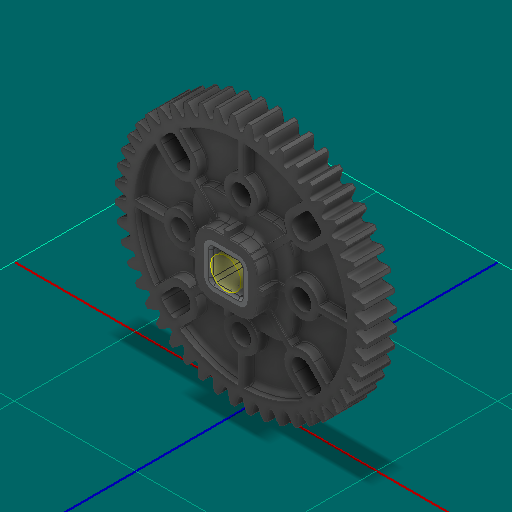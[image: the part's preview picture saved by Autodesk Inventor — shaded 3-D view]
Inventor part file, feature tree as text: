
AUTODESK INVENTOR PART (.ipt)
format: ipt  version: 2025 (Build 290162000, 162)  size: 3,893,248 bytes
history: native  units: in
note: dims shown in document units (in); Inventor stores cm internally (conversion verified against a paired STEP export)
features: other x6, sketch x3
ambient origin geometry x8: Origin, YZ Plane, XZ Plane, XY Plane, X Axis, Y Axis, Z Axis, Center Point
bodies: Solid1 (feature_tree), Solid2 (feature_tree)
feature tree (9):
  other  "Half Cut HS 48T Gear, No Insert.ipt"
  other  "Solid1::Half Cut HS 48T Gear, No Insert.ipt"
  other  "Solid2::Half Cut HS 48T Gear, No Insert.ipt"
  other  "TaggingFeature1"
  sketch  "Sketch1"  dims[d0=0.3937in]
  sketch  "Sketch2"
  sketch  "Sketch3"
  other  "Srf1"
  other  "Srf1::Derived"
